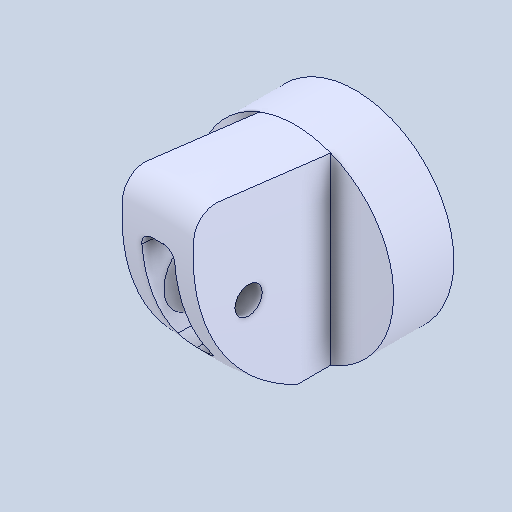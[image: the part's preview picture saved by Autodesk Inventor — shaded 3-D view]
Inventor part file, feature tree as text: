
AUTODESK INVENTOR PART (.ipt)
format: ipt  version: 2022 (Build 260153000, 153)  size: 170,496 bytes
history: mixed  units: mm
features: other x1, fillet x1, imported_body x1
ambient origin geometry x8: Origin, YZ Plane, XZ Plane, XY Plane, X Axis, Y Axis, Z Axis, Center Point
bodies: Body1 (imported_parasolid)
feature tree (3):
  other  "Sólido1"
  fillet  "Fillet2"  [1 undecoded]
  imported_body  NMx_Import_Brep_tag  [imported B-rep: ~5 faces, bbox_mm=None]
note: 1 required parameter value undecoded (feature->parameter linkage not recoverable at this tier; creation-order binding heuristic only, values carry confidence <= 0.55)
